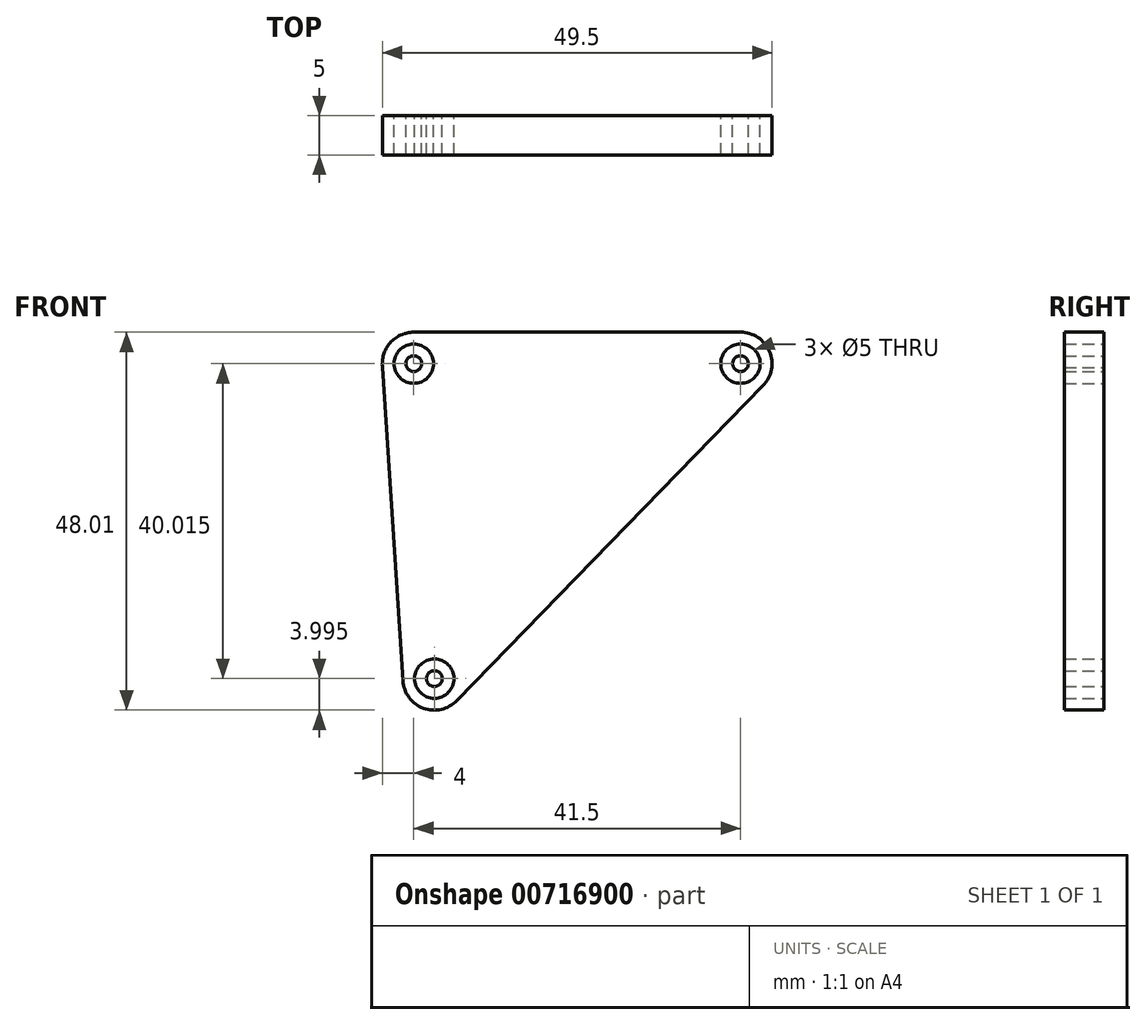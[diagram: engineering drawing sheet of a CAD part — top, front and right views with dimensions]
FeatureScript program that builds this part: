
annotation { "Feature Type Name" : "Feature", "Feature Type Description" : "" }
export const myFeature = defineFeature(function(context is Context, id is Id, definition is map)
    precondition{}
    {
        {
            var Q0;
            Q0=qCreatedBy(makeId("Front.planeOp"),FACE);
            var sketch = newSketch(context, id + "F0", { "sketchPlane" : qUnion([Q0])});
            skArc(sketch, "E0", {"start": v(0, 4) * mm, "mid": v(-3, 2.64) * mm, "end": v(-3.97, -0.52) * mm});
            skArc(sketch, "E1", {"start": v(44.37, -2.79) * mm, "mid": v(45.18, 1.56) * mm, "end": v(41.5, 4) * mm});
            skArc(sketch, "E2", {"start": v(-1.38, -40.27) * mm, "mid": v(1.23, -43.77) * mm, "end": v(5.48, -42.8) * mm});
            skLineSegment(sketch, "E3", {"start": v(0, 4) * mm, "end": v(41.5, 4) * mm});
            skLineSegment(sketch, "E4", {"start": v(-4, 0) * mm, "end": v(-1.38, -40.27) * mm});
            skLineSegment(sketch, "E5", {"start": v(44.37, -2.79) * mm, "end": v(5.48, -42.8) * mm});
            skCircle(sketch, "E6", {"center": v(0, 0) * mm, "radius": 2.5 * mm});
            skCircle(sketch, "E7", {"center": v(0, 0) * mm, "radius": 1 * mm});
            skCircle(sketch, "E8", {"center": v(41.5, 0) * mm, "radius": 2.5 * mm});
            skCircle(sketch, "E9", {"center": v(41.5, 0) * mm, "radius": 1 * mm});
            skCircle(sketch, "E10", {"center": v(2.6, -40.01) * mm, "radius": 2.5 * mm});
            skCircle(sketch, "E11", {"center": v(2.6, -40.01) * mm, "radius": 1 * mm});
            skSolve(sketch);
        }
        {
            var Q0;
            Q0 = qSketchRegion(id + "F0", true);
            var Q1;
            Q1=makeQuery(id+"F0.imprint","IMPRINT",FACE,{"disambiguationData":[TD([[makeQuery(id+"F0.imprint","IMPRINT",EDGE,{"derivedFrom":sQuery(id+"F0.wireOp",EDGE,"E7")}),1.0]])]});
            var Q2;
            Q2=makeQuery(id+"F0.imprint","IMPRINT",FACE,{"disambiguationData":[TD([[makeQuery(id+"F0.imprint","IMPRINT",EDGE,{"derivedFrom":sQuery(id+"F0.wireOp",EDGE,"E9")}),1.0]])]});
            var Q3;
            Q3=makeQuery(id+"F0.imprint","IMPRINT",FACE,{"disambiguationData":[TD([[makeQuery(id+"F0.imprint","IMPRINT",EDGE,{"derivedFrom":sQuery(id+"F0.wireOp",EDGE,"E11")}),1.0]])]});
            extrude(context, id + "F1", {"entities" : qUnion([Q0, Q1, Q2, Q3]), "depth" : 5 * mm, "offsetDistance" : 25.4 * mm});
        }
    });
